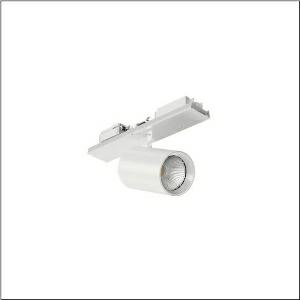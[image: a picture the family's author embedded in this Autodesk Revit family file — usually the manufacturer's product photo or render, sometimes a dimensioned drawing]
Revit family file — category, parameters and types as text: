
# Revit family: licross_r__spot_31_51sl13da43b_6d5a
name_source: partatom
category: Lighting Fixtures
units: mm (PartAtom-declared; Revit-internal decimal feet)

## family parameters
Cut with Voids When Loaded = No
Host = Face
Light Source = No
Part Type = Normal
Room Calculation Point = No
Round Connector Dimension = Use Diameter
Shared = No

## types (1)
- --- (1 x LED, 3680 lm, 28.6 W, 4000K)
    Apparent Load = 29 VA
    CIE Flux Codes = 92 97 99 100 100
    Color Rendering = 90
    Color Temperature = 4000K
    Default Elevation = 1800 mm
    Description = Licross® Spot 31, directional spotlight, light control with lens, of plastic, LED rated luminous flux: 3.680lm, light colour: 940, with plug, 5-pole, mains connection: 220..240V, AC, 50/60Hz, of aluminium, traffic white (RAL 9016), length: 300mm, diameter: 90mm, protection rating (complete): IP20, insulation class (complete): insulation class I (protective earthing), certification: CE, packaging unit: 1 piece
    Height = 175 mm
    Lamp = 1 x LED
    Lamp Light Flux = 3680 lm
    Lamp Power = 28.6 W
    Lamp count = 1
    Length = 90 mm
    Luminous efficacy = 129 lm/W
    Manufacturer = Siteco
    ModVariant = No
    Model = 51SL13DA43B
    Mounting Place = Ceiling
    Mounting Type = Pendant
    Number of Poles = 1
    OnlyDefault = Yes
    Power Factor = 1
    Product Name = Licross® Spot 31
    Product group = directional spotlight
    ProductGroupID = 905
    Protection Class = Protection class I
    Protection Degree = IP 20
    RLX_Detail_Level = 1
    RLX_Emergency_Light_Flux = 0 lm
    RLX_Emergency_Type = 0
    RLX_Emergency_Type_DB = No
    RlxData = <blob elided: 14809 chars, md5=6905688b>
    Socket = socket
    Standby Power = 0 W
    System Light Flux = 3680 lm
    System Power = 29 W
    Type Comments = factory setting: luminous flux: 100 % | (ON | ON | ON) | 700 mA
    Type Image = l_1245720.jpg
    URL = http://relux.com
    VarID = @adj_153711
    Voltage = 0 V
    Weight = 0.00 kg
    Width = 0 mm  [stored 0 ft]

note: [stored X ft] marks values corroborated as IEEE doubles in the binary element streams (Revit-internal decimal feet)

## geometry (parser evidence)
native form markers: Sweep x12
no freeform markers — native parametric forms only
